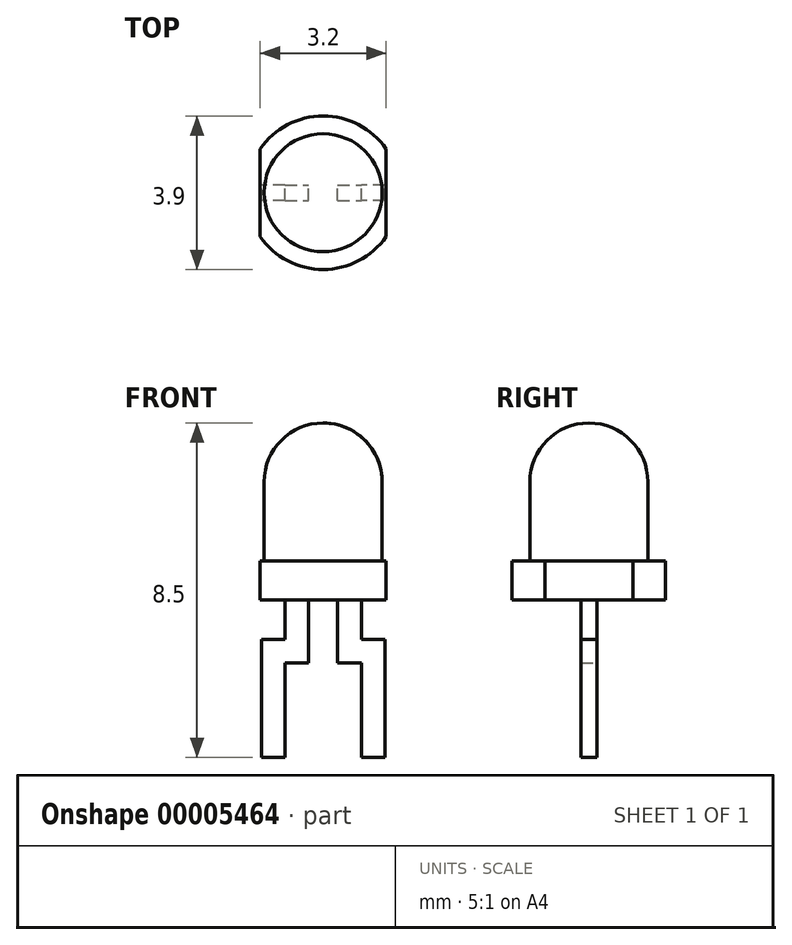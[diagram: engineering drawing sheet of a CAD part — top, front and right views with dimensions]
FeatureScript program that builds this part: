
annotation { "Feature Type Name" : "Feature", "Feature Type Description" : "" }
export const myFeature = defineFeature(function(context is Context, id is Id, definition is map)
    precondition{}
    {
        {
            var Q0;
            Q0=qCreatedBy(makeId("Front.planeOp"),FACE);
            var sketch = newSketch(context, id + "F0", { "sketchPlane" : qUnion([Q0])});
            skArc(sketch, "E0", {"start": v(0, 0) * mm, "mid": v(-1.06, -0.44) * mm, "end": v(-1.5, -1.5) * mm});
            skLineSegment(sketch, "E1", {"start": v(-1.5, -1.5) * mm, "end": v(-1.5, -3.5) * mm});
            skLineSegment(sketch, "E2", {"start": v(-1.5, -3.5) * mm, "end": v(-1.95, -3.5) * mm});
            skLineSegment(sketch, "E3", {"start": v(-1.95, -3.5) * mm, "end": v(-1.95, -4.5) * mm});
            skLineSegment(sketch, "E4", {"start": v(-1.95, -4.5) * mm, "end": v(0, -4.5) * mm});
            skLineSegment(sketch, "E5", {"start": v(0, 0) * mm, "end": v(0, -4.5) * mm});
            skLineSegment(sketch, "E6", {"start": v(-0.97, -4.5) * mm, "end": v(-0.97, -5.5) * mm});
            skLineSegment(sketch, "E7", {"start": v(-0.97, -5.5) * mm, "end": v(-1.57, -5.5) * mm});
            skLineSegment(sketch, "E8", {"start": v(-1.57, -5.5) * mm, "end": v(-1.57, -8.5) * mm});
            skLineSegment(sketch, "E9", {"start": v(-1.57, -8.5) * mm, "end": v(-0.97, -8.5) * mm});
            skLineSegment(sketch, "E10", {"start": v(-0.97, -8.5) * mm, "end": v(-0.97, -6.1) * mm});
            skLineSegment(sketch, "E11", {"start": v(-0.97, -6.1) * mm, "end": v(-0.37, -6.1) * mm});
            skLineSegment(sketch, "E12", {"start": v(-0.37, -6.1) * mm, "end": v(-0.37, -4.5) * mm});
            skPoint(sketch, "E13", {"position": v(-1.27, -8.5) * mm});
            skLineSegment(sketch, "E14.0.MirrorCS", {"start": v(0.97, -4.5) * mm, "end": v(0.97, -5.5) * mm});
            skLineSegment(sketch, "E14.1.MirrorCS", {"start": v(0.37, -6.1) * mm, "end": v(0.37, -4.5) * mm});
            skLineSegment(sketch, "E14.2.MirrorCS", {"start": v(0.97, -6.1) * mm, "end": v(0.37, -6.1) * mm});
            skLineSegment(sketch, "E14.3.MirrorCS", {"start": v(0.97, -5.5) * mm, "end": v(1.57, -5.5) * mm});
            skLineSegment(sketch, "E14.4.MirrorCS", {"start": v(0.97, -8.5) * mm, "end": v(0.97, -6.1) * mm});
            skLineSegment(sketch, "E14.5.MirrorCS", {"start": v(1.57, -5.5) * mm, "end": v(1.57, -8.5) * mm});
            skLineSegment(sketch, "E14.6.MirrorCS", {"start": v(1.57, -8.5) * mm, "end": v(0.97, -8.5) * mm});
            skLineSegment(sketch, "E15", {"start": v(0.37, -4.5) * mm, "end": v(0.97, -4.5) * mm});
            skLineSegment(sketch, "E16", {"start": v(-1.6, -4.5) * mm, "end": v(-1.6, -3.5) * mm});
            skLineSegment(sketch, "E17.0.MirrorCS", {"start": v(1.6, -4.5) * mm, "end": v(1.6, -3.5) * mm});
            skLineSegment(sketch, "E17.1.MirrorCS", {"start": v(1.95, -3.5) * mm, "end": v(1.95, -4.5) * mm});
            skLineSegment(sketch, "E18", {"start": v(1.6, -3.5) * mm, "end": v(1.95, -3.5) * mm});
            skLineSegment(sketch, "E19", {"start": v(1.6, -4.5) * mm, "end": v(1.95, -4.5) * mm});
            skSolve(sketch);
        }
        {
            var Q0;
            Q0=makeQuery(id+"F0.imprint","IMPRINT",FACE,{"disambiguationData":[TD([[makeQuery(id+"F0.imprint","IMPRINT",EDGE,{"derivedFrom":sQuery(id+"F0.wireOp",EDGE,"E0")}),1.0]])]});
            var Q1;
            {var subQ2=sQuery(id+"F0.wireOp",EDGE,"E3");Q1=makeQuery(id+"F0.imprint","IMPRINT",FACE,{"disambiguationData":[TD([[makeQuery(id+"F0.imprint","IMPRINT",EDGE,{"derivedFrom":subQ2}),1.0]])]});}
            var Q2;
            Q2=sQuery(id+"F0.wireOp",EDGE,"E5");
            revolve(context, id + "F1", {"entities" : qUnion([Q0, Q1]), "axis" : qUnion([Q2]), "revolveType" : RevolveType.FULL});
        }
        {
            var Q0;
            {var subQ2=sQuery(id+"F0.wireOp",EDGE,"E3");Q0=makeQuery(id+"F0.imprint","IMPRINT",FACE,{"disambiguationData":[TD([[makeQuery(id+"F0.imprint","IMPRINT",EDGE,{"derivedFrom":subQ2}),1.0]])]});}
            var Q1;
            Q1=makeQuery(id+"F0.imprint","IMPRINT",FACE,{"disambiguationData":[TD([[makeQuery(id+"F0.imprint","IMPRINT",EDGE,{"derivedFrom":sQuery(id+"F0.wireOp",EDGE,"E17.0.MirrorCS")}),-1.0]])]});
            extrude(context, id + "F2", {"entities" : qUnion([Q0, Q1]), "operationType" : NewBodyOperationType.REMOVE, "endBound" : BoundingType.THROUGH_ALL, "oppositeDirection" : true, "depth" : 25 * mm, "hasSecondDirection" : true, "secondDirectionBound" : BoundingType.THROUGH_ALL, "secondDirectionOppositeDirection" : false, "secondDirectionDepth" : 25 * mm});
        }
        {
            var Q0;
            Q0=makeQuery(id+"F0.imprint","IMPRINT",FACE,{"disambiguationData":[TD([[makeQuery(id+"F0.imprint","IMPRINT",EDGE,{"derivedFrom":sQuery(id+"F0.wireOp",EDGE,"E14.0.MirrorCS")}),-1.0]])]});
            var Q1;
            {var subQ1=sQuery(id+"F0.wireOp",EDGE,"E6");Q1=makeQuery(id+"F0.imprint","IMPRINT",FACE,{"disambiguationData":[TD([[makeQuery(id+"F0.imprint","IMPRINT",EDGE,{"derivedFrom":subQ1}),1.0]])]});}
            extrude(context, id + "F3", {"entities" : qUnion([Q0, Q1]), "operationType" : NewBodyOperationType.ADD, "depth" : .4 * mm, "symmetric" : true});
        }
    });
